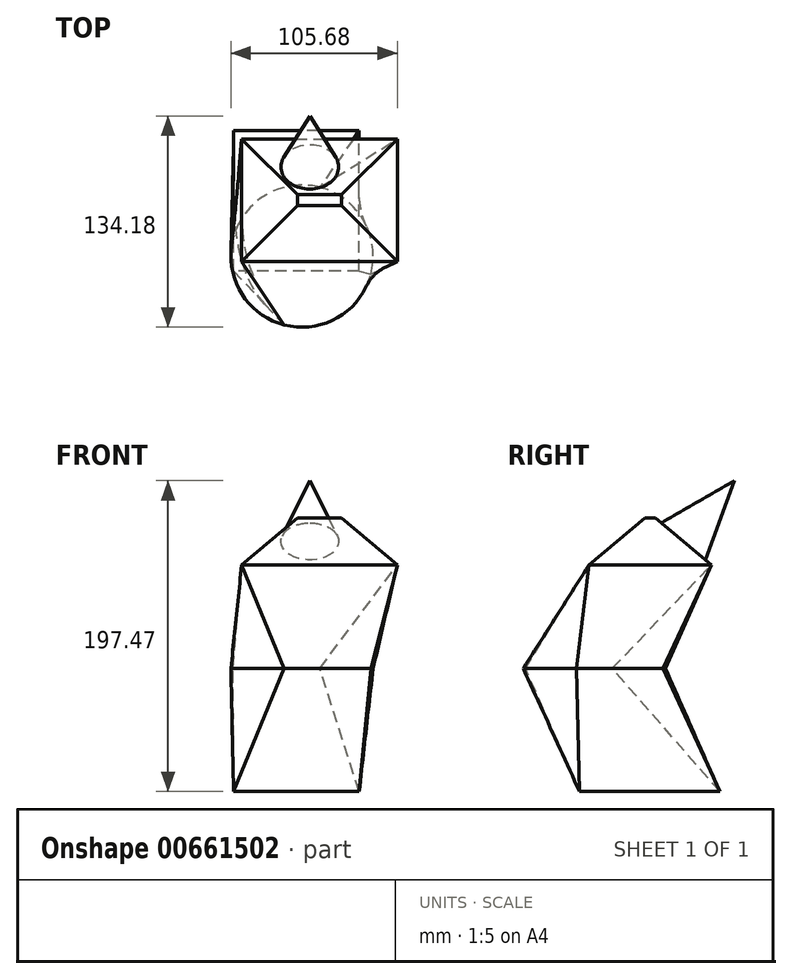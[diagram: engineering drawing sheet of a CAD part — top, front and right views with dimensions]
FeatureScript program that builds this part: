
annotation { "Feature Type Name" : "Feature", "Feature Type Description" : "" }
export const myFeature = defineFeature(function(context is Context, id is Id, definition is map)
    precondition{}
    {
        {
            var Q0;
            Q0=qCreatedBy(makeId("Top.planeOp"),FACE);
            cPlane(context, id + "F0", {"entities" : qUnion([Q0]), "cplaneType" : CPlaneType.OFFSET, "offset" : 78.23 * mm, "width" : 152.4 * mm, "height" : 152.4 * mm});
        }
        {
            var Q0;
            Q0=qCreatedBy(makeId("Top.planeOp"),FACE);
            var sketch = newSketch(context, id + "F1", { "sketchPlane" : qUnion([Q0])});
            skLineSegment(sketch, "E0.bottom", {"start": v(31.36, -34.04) * mm, "end": v(-48.44, -34.04) * mm});
            skLineSegment(sketch, "E0.top", {"start": v(31.36, 55.03) * mm, "end": v(-48.44, 55.03) * mm});
            skLineSegment(sketch, "E0.left", {"start": v(31.36, -34.04) * mm, "end": v(31.36, 55.03) * mm});
            skLineSegment(sketch, "E0.right", {"start": v(-48.44, -34.04) * mm, "end": v(-48.44, 55.03) * mm});
            skSolve(sketch);
        }
        {
            var Q0;
            Q0=qCreatedBy(id+"F0.planeOp",FACE);
            var sketch = newSketch(context, id + "F2", { "sketchPlane" : qUnion([Q0])});
            skCircle(sketch, "E1", {"center": v(-4.94, -24.64) * mm, "radius": 45.15 * mm});
            skSolve(sketch);
        }
        {
            var Q0;
            Q0=makeQuery(id+"F1.imprint","IMPRINT",FACE,{"disambiguationData":[TD([[makeQuery(id+"F1.imprint","IMPRINT",EDGE,{"derivedFrom":sQuery(id+"F1.wireOp",EDGE,"E0.bottom")}),-1.0]])]});
            var Q1;
            Q1=makeQuery(id+"F2.imprint","IMPRINT",FACE,{"disambiguationData":[TD([[makeQuery(id+"F2.imprint","IMPRINT",EDGE,{"derivedFrom":sQuery(id+"F2.wireOp",EDGE,"E1")}),1.0]])]});
            loft(context, id + "F3", {"sheetProfilesArray" : [{ "sheetProfileEntities" : qUnion([Q0]) }, { "sheetProfileEntities" : qUnion([Q1]) }]});
        }
        {
            var Q0;
            Q0=qCreatedBy(id+"F0.planeOp",FACE);
            cPlane(context, id + "F4", {"entities" : qUnion([Q0]), "cplaneType" : CPlaneType.OFFSET, "offset" : 65.8 * mm, "width" : 152.4 * mm, "height" : 152.4 * mm});
        }
        {
            var Q0;
            Q0=qCreatedBy(id+"F4.planeOp",FACE);
            var sketch = newSketch(context, id + "F5", { "sketchPlane" : qUnion([Q0])});
            skLineSegment(sketch, "E2.bottom", {"start": v(-43.26, 49.71) * mm, "end": v(55.59, 49.71) * mm});
            skLineSegment(sketch, "E2.top", {"start": v(-43.26, -28.06) * mm, "end": v(55.59, -28.06) * mm});
            skLineSegment(sketch, "E2.left", {"start": v(-43.26, 49.71) * mm, "end": v(-43.26, -28.06) * mm});
            skLineSegment(sketch, "E2.right", {"start": v(55.59, 49.71) * mm, "end": v(55.59, -28.06) * mm});
            skSolve(sketch);
        }
        {
            var Q1;
            Q1=makeQuery(id+"F3.opLoft","CAP_FACE",FACE,{"disambiguationData":[OSD([makeQuery(id+"F2.imprint","IMPRINT",FACE,{"disambiguationData":[TD([[makeQuery(id+"F2.imprint","IMPRINT",EDGE,{"derivedFrom":sQuery(id+"F2.wireOp",EDGE,"E1")}),1.0]])]})])],"isStart":true});
            var Q2;
            Q2=makeQuery(id+"F5.imprint","IMPRINT",FACE,{"disambiguationData":[TD([[makeQuery(id+"F5.imprint","IMPRINT",EDGE,{"derivedFrom":sQuery(id+"F5.wireOp",EDGE,"E2.bottom")}),-1.0]])]});
            loft(context, id + "F6", {"operationType" : NewBodyOperationType.ADD, "sheetProfilesArray" : [{ "sheetProfileEntities" : qUnion([Q1]) }, { "sheetProfileEntities" : qUnion([Q2]) }]});
        }
        {
            var Q0;
            Q0=makeQuery(id+"F6.opLoft","CAP_FACE",FACE,{"disambiguationData":[OSD([makeQuery(id+"F5.imprint","IMPRINT",FACE,{"disambiguationData":[TD([[makeQuery(id+"F5.imprint","IMPRINT",EDGE,{"derivedFrom":sQuery(id+"F5.wireOp",EDGE,"E2.bottom")}),-1.0]])]})])],"isStart":true});
            extrude(context, id + "F7", {"entities" : qUnion([Q0]), "depth" : 29.72 * mm, "offsetDistance" : 25.4 * mm, "hasDraft" : true, "draftAngle" : 50 * degree, "draftPullDirection" : true});
        }
        {
            var Q0;
            Q0=makeQuery(id+"F7.opExtrude","SWEPT_FACE",FACE,{"disambiguationData":[OSD([sQuery(id+"F5.wireOp",EDGE,"E2.bottom"),sQuery(id+"F5.wireOp",EDGE,"E2.left"),sQuery(id+"F5.wireOp",EDGE,"E2.right")])]});
            var sketch = newSketch(context, id + "F8", { "sketchPlane" : qUnion([Q0])});
            skCircle(sketch, "E3", {"center": v(0, -77.6) * mm, "radius": 18.34 * mm});
            skPoint(sketch, "E3.centerSnap0", {"position": v(37.88, -77.6) * mm});
            skSolve(sketch);
        }
        {
            var Q0;
            Q0=makeQuery(id+"F8.imprint","IMPRINT",FACE,{"disambiguationData":[TD([[makeQuery(id+"F8.imprint","IMPRINT",EDGE,{"derivedFrom":sQuery(id+"F8.wireOp",EDGE,"E3")}),1.0]])]});
            extrude(context, id + "F9", {"entities" : qUnion([Q0]), "operationType" : NewBodyOperationType.ADD, "depth" : 96.52 * mm, "offsetDistance" : 25.4 * mm, "hasDraft" : true, "draftAngle" : 20 * degree, "draftPullDirection" : true});
        }
    });
